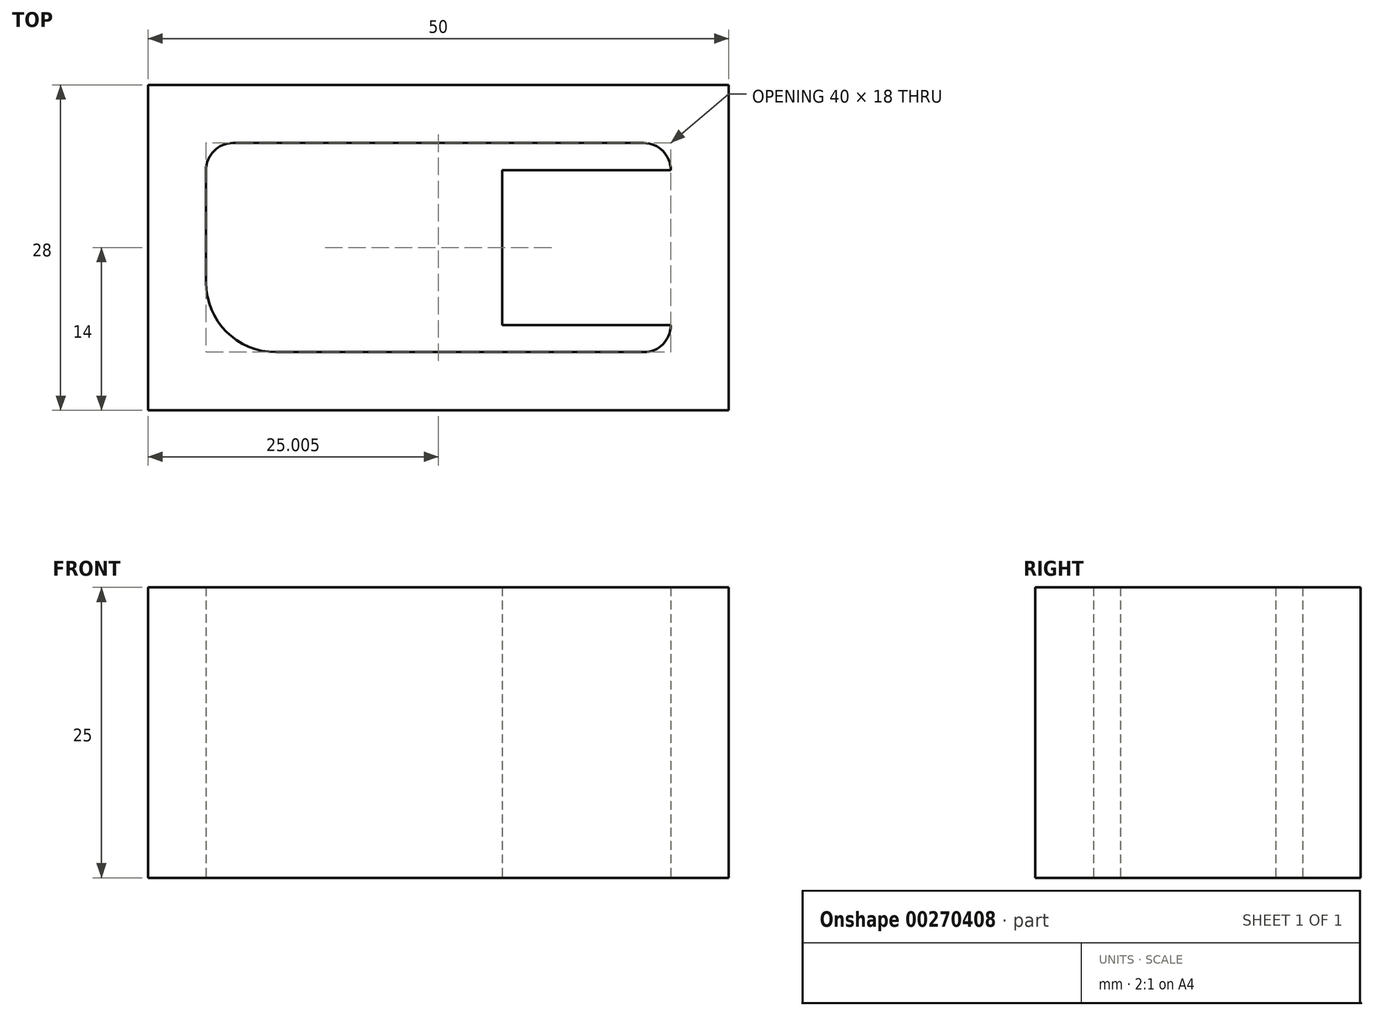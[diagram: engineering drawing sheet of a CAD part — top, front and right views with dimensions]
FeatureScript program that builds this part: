
annotation { "Feature Type Name" : "Feature", "Feature Type Description" : "" }
export const myFeature = defineFeature(function(context is Context, id is Id, definition is map)
    precondition{}
    {
        {
            var Q0;
            Q0=qCreatedBy(makeId("Top.planeOp"),FACE);
            var sketch = newSketch(context, id + "F0", { "sketchPlane" : qUnion([Q0])});
            skLineSegment(sketch, "E0.bottom", {"start": v(-53.83, 50.35) * mm, "end": v(-18.46, 50.35) * mm});
            skLineSegment(sketch, "E0.top", {"start": v(-50.15, 32.35) * mm, "end": v(-18.46, 32.35) * mm});
            skLineSegment(sketch, "E0.left", {"start": v(-56.15, 48.03) * mm, "end": v(-56.15, 38.35) * mm});
            skLineSegment(sketch, "E0.right", {"start": v(-16.15, 48.03) * mm, "end": v(-16.15, 34.67) * mm});
            skPoint(sketch, "E1.visualSharp", {"position": v(-56.15, 50.35) * mm});
            skArc(sketch, "E1.filletArc", {"start": v(-53.83, 50.35) * mm, "mid": v(-55.47, 49.67) * mm, "end": v(-56.15, 48.03) * mm});
            skPoint(sketch, "E2.visualSharp", {"position": v(-16.15, 50.35) * mm});
            skArc(sketch, "E2.filletArc", {"start": v(-16.15, 48.03) * mm, "mid": v(-16.82, 49.67) * mm, "end": v(-18.46, 50.35) * mm});
            skPoint(sketch, "E3.visualSharp", {"position": v(-16.15, 32.35) * mm});
            skArc(sketch, "E3.filletArc", {"start": v(-18.46, 32.35) * mm, "mid": v(-16.82, 33.03) * mm, "end": v(-16.15, 34.67) * mm});
            skPoint(sketch, "E4.visualSharp", {"position": v(-56.15, 32.35) * mm});
            skArc(sketch, "E4.filletArc", {"start": v(-56.15, 38.35) * mm, "mid": v(-54.39, 34.1) * mm, "end": v(-50.15, 32.35) * mm});
            skLineSegment(sketch, "E5.0", {"start": v(-61.15, 55.35) * mm, "end": v(-11.15, 55.35) * mm});
            skLineSegment(sketch, "E5.1", {"start": v(-61.15, 55.35) * mm, "end": v(-61.15, 27.35) * mm});
            skLineSegment(sketch, "E5.2", {"start": v(-61.15, 27.35) * mm, "end": v(-11.15, 27.35) * mm});
            skLineSegment(sketch, "E5.3", {"start": v(-11.15, 55.35) * mm, "end": v(-11.15, 27.35) * mm});
            skSolve(sketch);
        }
        {
            var Q0;
            Q0=makeQuery(id+"F0.imprint","IMPRINT",FACE,{"disambiguationData":[TD([[makeQuery(id+"F0.imprint","IMPRINT",EDGE,{"derivedFrom":sQuery(id+"F0.wireOp",EDGE,"E0.bottom")}),1.0]])]});
            extrude(context, id + "F1", {"entities" : qUnion([Q0]), "depth" : 25 * mm, "offsetDistance" : 25 * mm});
        }
        {
            var Q0;
            Q0=makeQuery(id+"F1.opExtrude","SWEPT_FACE",FACE,{"disambiguationData":[OSD([sQuery(id+"F0.wireOp",EDGE,"E0.right")])]});
            extrude(context, id + "F2", {"entities" : qUnion([Q0]), "operationType" : NewBodyOperationType.ADD, "depth" : 14.5 * mm, "offsetDistance" : 25 * mm});
        }
    });
